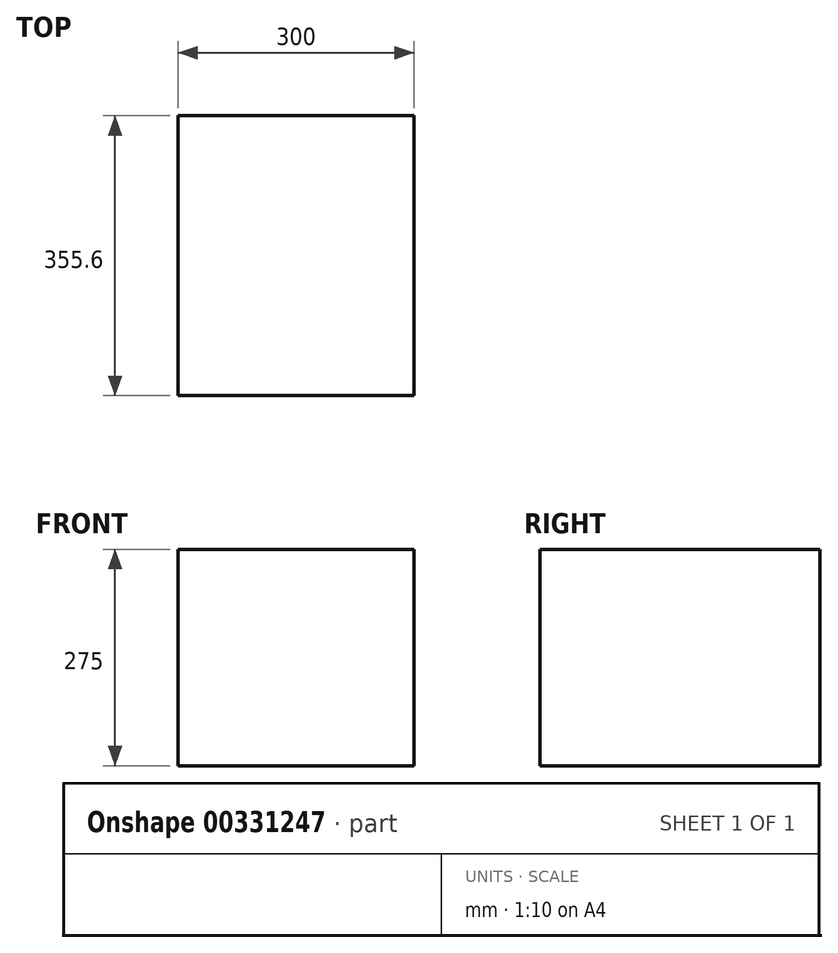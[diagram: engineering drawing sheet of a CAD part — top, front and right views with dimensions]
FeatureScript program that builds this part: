
annotation { "Feature Type Name" : "Feature", "Feature Type Description" : "" }
export const myFeature = defineFeature(function(context is Context, id is Id, definition is map)
    precondition{}
    {
        {
            var Q0;
            Q0=qCreatedBy(makeId("Front.planeOp"),FACE);
            var sketch = newSketch(context, id + "F0", { "sketchPlane" : qUnion([Q0])});
            skLineSegment(sketch, "E0.bottom", {"start": v(-150, 137.5) * mm, "end": v(150, 137.5) * mm});
            skLineSegment(sketch, "E0.top", {"start": v(-150, -137.5) * mm, "end": v(150, -137.5) * mm});
            skLineSegment(sketch, "E0.left", {"start": v(-150, 137.5) * mm, "end": v(-150, -137.5) * mm});
            skLineSegment(sketch, "E0.right", {"start": v(150, 137.5) * mm, "end": v(150, -137.5) * mm});
            skPoint(sketch, "E0.middle", {"position": v(0, 0) * mm});
            skSolve(sketch);
        }
        {
            var Q0;
            Q0 = qSketchRegion(id + "F0", true);
            extrude(context, id + "F1", {"entities" : qUnion([Q0]), "endBound" : BoundingType.SYMMETRIC, "depth" : 355.6 * mm});
        }
    });
